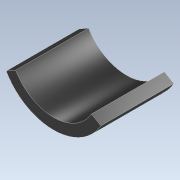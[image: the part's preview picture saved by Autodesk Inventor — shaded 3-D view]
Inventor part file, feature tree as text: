
AUTODESK INVENTOR PART (.ipt)
format: ipt  version: 2022 (Build 260153000, 153)  size: 89,600 bytes
history: native  units: mm
features: extrude x1, sketch x1
ambient origin geometry x8: Origin, YZ Plane, XZ Plane, XY Plane, X Axis, Y Axis, Z Axis, Center Point
bodies: Solid1 (feature_tree)
feature tree (2):
  extrude  "Extrusion1"  TaperAngle=30.0deg  [1 undecoded]
  sketch  "Sketch1"  dims[d0=15.0mm d1=30.0deg d2=120.0deg d3=12.0mm d4=20.0mm d5=0.0mm]
note: 1 required parameter value undecoded (feature->parameter linkage not recoverable at this tier; creation-order binding heuristic only, values carry confidence <= 0.55)
